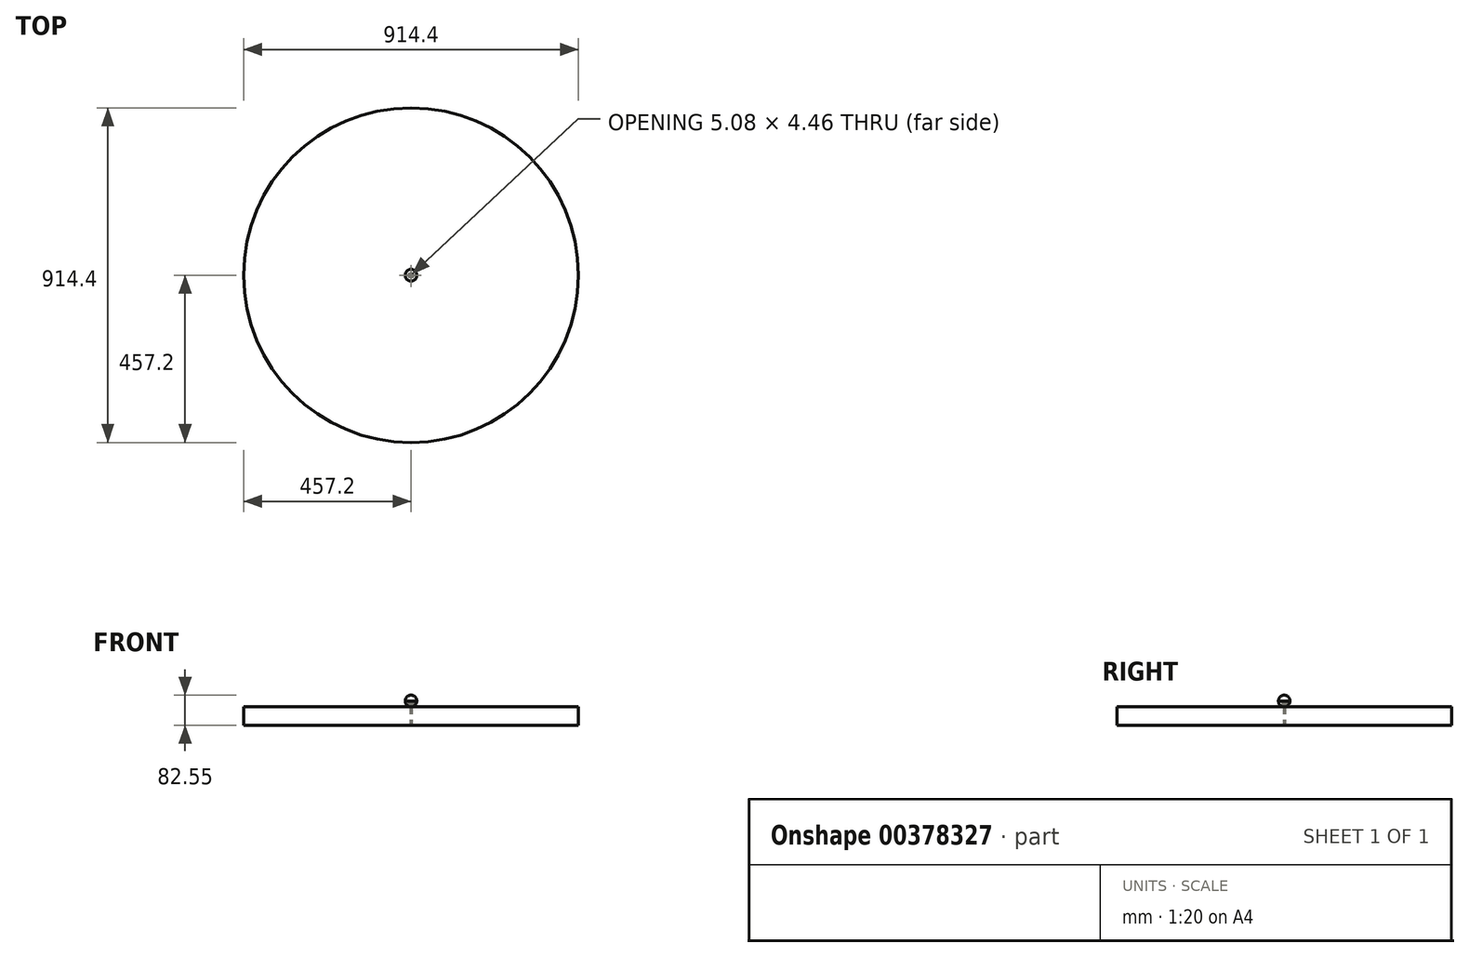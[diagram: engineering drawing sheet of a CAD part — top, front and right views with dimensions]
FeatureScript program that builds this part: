
annotation { "Feature Type Name" : "Feature", "Feature Type Description" : "" }
export const myFeature = defineFeature(function(context is Context, id is Id, definition is map)
    precondition{}
    {
        {
            var Q0;
            Q0=qCreatedBy(makeId("Top.planeOp"),FACE);
            var sketch = newSketch(context, id + "F0", { "sketchPlane" : qUnion([Q0])});
            skCircle(sketch, "E0", {"center": v(0, 0) * mm, "radius": 457.2 * mm});
            skCircle(sketch, "E1.cCircle", {"center": v(0, 0) * mm, "radius": 6.6 * mm, "construction": true});
            skLineSegment(sketch, "E1.0", {"start": v(3.81, 6.6) * mm, "end": v(7.62, 0) * mm});
            skLineSegment(sketch, "E1.1", {"start": v(7.62, 0) * mm, "end": v(3.81, -6.6) * mm});
            skLineSegment(sketch, "E1.2", {"start": v(3.8, -6.6) * mm, "end": v(-3.8, -6.6) * mm});
            skLineSegment(sketch, "E1.3", {"start": v(-3.81, -6.6) * mm, "end": v(-7.62, 0) * mm});
            skLineSegment(sketch, "E1.4", {"start": v(-7.62, 0) * mm, "end": v(-3.81, 6.6) * mm});
            skLineSegment(sketch, "E1.5", {"start": v(-3.8, 6.6) * mm, "end": v(3.8, 6.6) * mm});
            skCircle(sketch, "E2.cCircle", {"center": v(0, 0) * mm, "radius": 2.2 * mm, "construction": true});
            skLineSegment(sketch, "E2.0", {"start": v(1.32, 2.17) * mm, "end": v(2.54, -0.06) * mm});
            skLineSegment(sketch, "E2.1", {"start": v(2.54, -0.06) * mm, "end": v(1.22, -2.23) * mm});
            skLineSegment(sketch, "E2.2", {"start": v(1.22, -2.23) * mm, "end": v(-1.32, -2.17) * mm});
            skLineSegment(sketch, "E2.3", {"start": v(-1.32, -2.17) * mm, "end": v(-2.54, 0.06) * mm});
            skLineSegment(sketch, "E2.4", {"start": v(-2.54, 0.06) * mm, "end": v(-1.22, 2.23) * mm});
            skLineSegment(sketch, "E2.5", {"start": v(-1.22, 2.23) * mm, "end": v(1.32, 2.17) * mm});
            skPoint(sketch, "E2.0.midPoint", {"position": v(1.93, 1.05) * mm});
            skSolve(sketch);
        }
        {
            var Q0;
            Q0=makeQuery(id+"F0.imprint","IMPRINT",FACE,{"disambiguationData":[TD([[makeQuery(id+"F0.imprint","IMPRINT",EDGE,{"derivedFrom":sQuery(id+"F0.wireOp",EDGE,"E0")}),1.0]])]});
            extrude(context, id + "F1", {"entities" : qUnion([Q0]), "depth" : 50.8 * mm});
        }
        {
            var Q0;
            Q0=makeQuery(id+"F0.imprint","IMPRINT",FACE,{"disambiguationData":[TD([[makeQuery(id+"F0.imprint","IMPRINT",EDGE,{"derivedFrom":sQuery(id+"F0.wireOp",EDGE,"E1.0")}),-1.0]])]});
            extrude(context, id + "F2", {"entities" : qUnion([Q0]), "operationType" : NewBodyOperationType.ADD, "depth" : 60.96 * mm});
        }
        {
            var Q0;
            Q0=makeQuery(id+"F1.opExtrude","CAP_FACE",FACE,{"disambiguationData":[OSD([sQuery(id+"F0.wireOp",EDGE,"E0"),sQuery(id+"F0.wireOp",EDGE,"E1.0"),sQuery(id+"F0.wireOp",EDGE,"E1.1"),sQuery(id+"F0.wireOp",EDGE,"E1.2"),sQuery(id+"F0.wireOp",EDGE,"E1.3"),sQuery(id+"F0.wireOp",EDGE,"E1.4"),sQuery(id+"F0.wireOp",EDGE,"E1.5")])],"isStart":false});
            var sketch = newSketch(context, id + "F3", { "sketchPlane" : qUnion([Q0])});
            skCircle(sketch, "E3", {"center": v(0, 0) * mm, "radius": 15.88 * mm});
            skSolve(sketch);
        }
        {
            var Q0;
            Q0 = qSketchRegion(id + "F3", true);
            extrude(context, id + "F4", {"entities" : qUnion([Q0]), "depth" : 31.75 * mm, "hasSecondDirection" : true, "secondDirectionOppositeDirection" : false, "secondDirectionDepth" : 0 * mm});
        }
        {
            var Q0;
            Q0=makeQuery(id+"F4.opExtrude","CAP_EDGE",EDGE,{"disambiguationData":[OSD([sQuery(id+"F3.wireOp",EDGE,"E3")])],"isStart":false});
            var Q1;
            Q1=makeQuery(id+"F4.opExtrude","CAP_EDGE",EDGE,{"disambiguationData":[OSD([sQuery(id+"F3.wireOp",EDGE,"E3")])],"isStart":true});
            fillet(context, id + "F5", {"entities" : qUnion([Q0, Q1]), "radius" : 15.85 * mm, "tangentPropagation" : true, "allowEdgeOverflow" : false});
        }
    });
